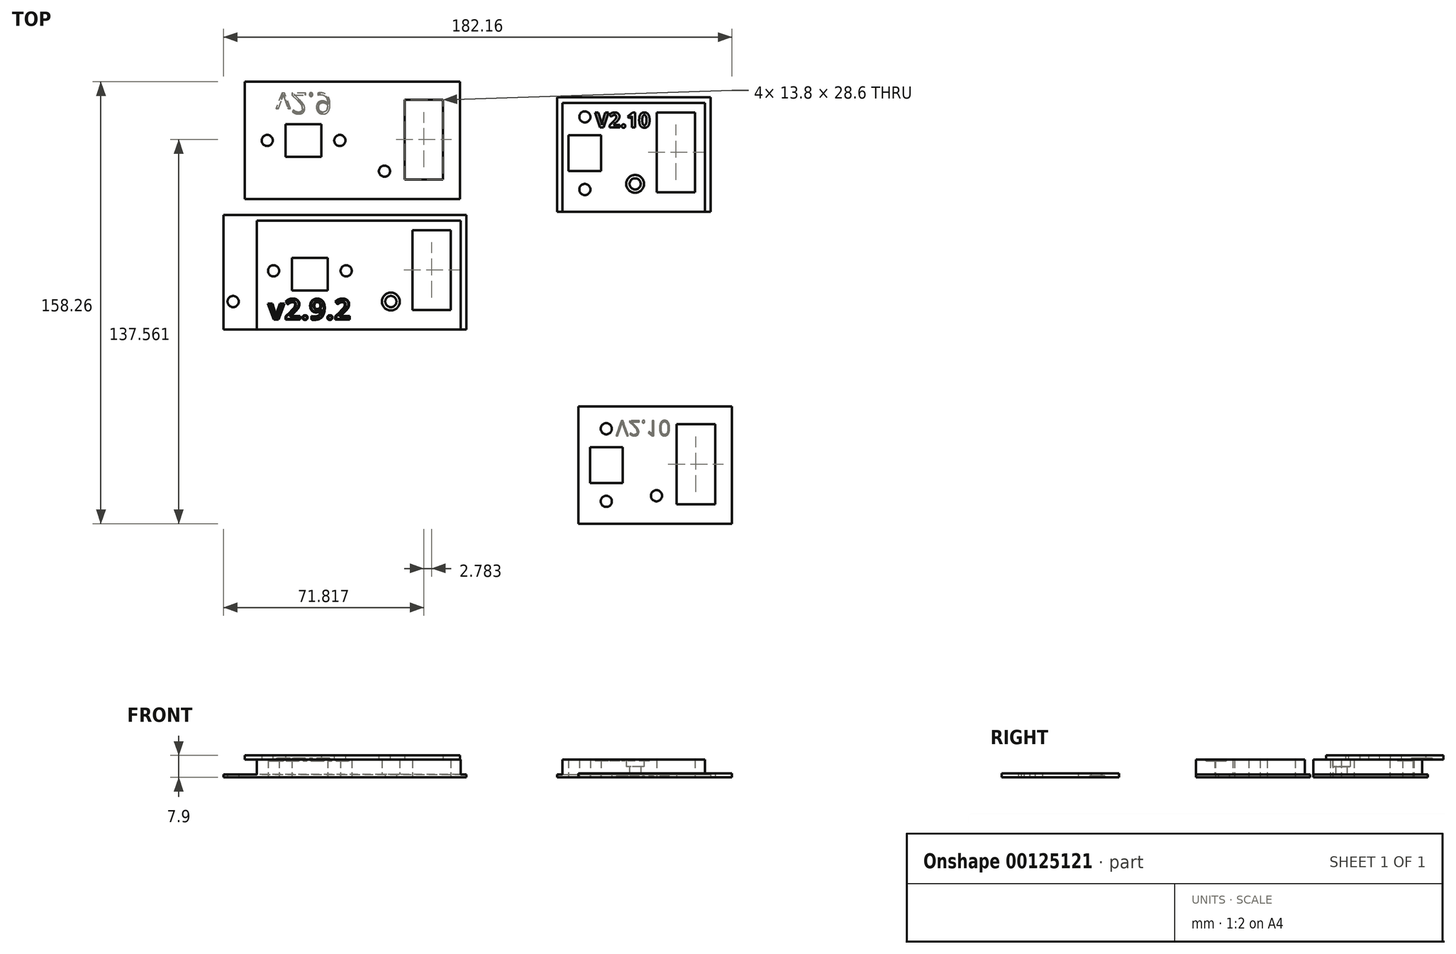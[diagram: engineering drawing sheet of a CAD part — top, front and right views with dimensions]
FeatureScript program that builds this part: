
annotation { "Feature Type Name" : "Feature", "Feature Type Description" : "" }
export const myFeature = defineFeature(function(context is Context, id is Id, definition is map)
    precondition{}
    {
        {
            var Q0;
            Q0=qCreatedBy(makeId("Top.planeOp"),FACE);
            var sketch = newSketch(context, id + "F0", { "sketchPlane" : qUnion([Q0])});
            skLineSegment(sketch, "E0.bottom", {"start": v(-50.93, -1.14) * mm, "end": v(36.07, -1.14) * mm});
            skLineSegment(sketch, "E0.left", {"start": v(-50.93, -1.14) * mm, "end": v(-50.93, -42.14) * mm});
            skLineSegment(sketch, "E0.right", {"start": v(36.07, -1.14) * mm, "end": v(36.07, -42.14) * mm});
            skLineSegment(sketch, "E1", {"start": v(-50.93, -42.14) * mm, "end": v(-38.93, -42.14) * mm});
            skLineSegment(sketch, "E2", {"start": v(-38.93, -42.14) * mm, "end": v(-32.93, -42.14) * mm});
            skLineSegment(sketch, "E3", {"start": v(-32.93, -42.14) * mm, "end": v(-6.93, -42.14) * mm});
            skLineSegment(sketch, "E4", {"start": v(-6.93, -42.14) * mm, "end": v(9.07, -42.14) * mm});
            skLineSegment(sketch, "E5", {"start": v(9.07, -42.14) * mm, "end": v(34.07, -42.14) * mm});
            skLineSegment(sketch, "E6", {"start": v(34.07, -42.14) * mm, "end": v(36.07, -42.14) * mm});
            skLineSegment(sketch, "E7", {"start": v(34.07, -42.14) * mm, "end": v(34.07, -3.14) * mm});
            skLineSegment(sketch, "E8", {"start": v(34.07, -3.14) * mm, "end": v(-38.93, -3.14) * mm});
            skLineSegment(sketch, "E9", {"start": v(-38.93, -3.14) * mm, "end": v(-38.93, -42.14) * mm});
            skLineSegment(sketch, "E10", {"start": v(-38.93, -42.14) * mm, "end": v(-47.43, -42.14) * mm, "construction": true});
            skLineSegment(sketch, "E11", {"start": v(-47.43, -42.14) * mm, "end": v(-47.43, -32.14) * mm, "construction": true});
            skCircle(sketch, "E12", {"center": v(-47.43, -32.14) * mm, "radius": 2 * mm});
            skLineSegment(sketch, "E13", {"start": v(-32.93, -42.14) * mm, "end": v(-32.93, -21.14) * mm, "construction": true});
            skLineSegment(sketch, "E14", {"start": v(-6.93, -42.14) * mm, "end": v(-6.93, -21.14) * mm, "construction": true});
            skLineSegment(sketch, "E15", {"start": v(9.07, -42.14) * mm, "end": v(9.07, -32.14) * mm, "construction": true});
            skCircle(sketch, "E16", {"center": v(9.07, -32.14) * mm, "radius": 2 * mm});
            skCircle(sketch, "E17", {"center": v(-32.93, -21.14) * mm, "radius": 2 * mm});
            skCircle(sketch, "E18", {"center": v(-6.93, -21.14) * mm, "radius": 2 * mm});
            skLineSegment(sketch, "E19.bottom", {"start": v(-26.33, -16.54) * mm, "end": v(-13.53, -16.54) * mm});
            skLineSegment(sketch, "E19.top", {"start": v(-26.33, -28.24) * mm, "end": v(-13.53, -28.24) * mm});
            skLineSegment(sketch, "E19.left", {"start": v(-26.33, -16.54) * mm, "end": v(-26.33, -28.24) * mm});
            skLineSegment(sketch, "E19.right", {"start": v(-13.53, -16.54) * mm, "end": v(-13.53, -28.24) * mm});
            skLineSegment(sketch, "E20", {"start": v(-32.93, -21.14) * mm, "end": v(-26.33, -21.14) * mm, "construction": true});
            skLineSegment(sketch, "E21", {"start": v(-6.93, -21.14) * mm, "end": v(-13.53, -21.14) * mm, "construction": true});
            skLineSegment(sketch, "E22", {"start": v(-19.93, -28.24) * mm, "end": v(-19.93, -42.14) * mm, "construction": true});
            skLineSegment(sketch, "E23.bottom", {"start": v(16.77, -6.54) * mm, "end": v(30.57, -6.54) * mm});
            skLineSegment(sketch, "E23.top", {"start": v(16.77, -35.14) * mm, "end": v(30.57, -35.14) * mm});
            skLineSegment(sketch, "E23.left", {"start": v(16.77, -6.54) * mm, "end": v(16.77, -35.14) * mm});
            skLineSegment(sketch, "E23.right", {"start": v(30.57, -6.54) * mm, "end": v(30.57, -35.14) * mm});
            skLineSegment(sketch, "E24", {"start": v(34.07, -42.14) * mm, "end": v(30.57, -42.14) * mm, "construction": true});
            skLineSegment(sketch, "E25", {"start": v(30.57, -42.14) * mm, "end": v(30.57, -35.14) * mm, "construction": true});
            skSolve(sketch);
        }
        {
            var Q0;
            Q0 = qSketchRegion(id + "F0", true);
            extrude(context, id + "F1", {"entities" : qUnion([Q0]), "depth" : 1 * mm});
        }
        {
            var Q0;
            Q0=makeQuery(id+"F1.opExtrude","CAP_FACE",FACE,{"disambiguationData":[OSD([sQuery(id+"F0.wireOp",EDGE,"E0.bottom"),sQuery(id+"F0.wireOp",EDGE,"E0.left"),sQuery(id+"F0.wireOp",EDGE,"E0.right"),sQuery(id+"F0.wireOp",EDGE,"E1"),sQuery(id+"F0.wireOp",EDGE,"E2"),sQuery(id+"F0.wireOp",EDGE,"E3"),sQuery(id+"F0.wireOp",EDGE,"E4"),sQuery(id+"F0.wireOp",EDGE,"E5"),sQuery(id+"F0.wireOp",EDGE,"E6"),sQuery(id+"F0.wireOp",EDGE,"E12"),sQuery(id+"F0.wireOp",EDGE,"E16"),sQuery(id+"F0.wireOp",EDGE,"E17"),sQuery(id+"F0.wireOp",EDGE,"E18"),sQuery(id+"F0.wireOp",EDGE,"E19.bottom"),sQuery(id+"F0.wireOp",EDGE,"E19.top"),sQuery(id+"F0.wireOp",EDGE,"E19.left"),sQuery(id+"F0.wireOp",EDGE,"E19.right"),sQuery(id+"F0.wireOp",EDGE,"E23.bottom"),sQuery(id+"F0.wireOp",EDGE,"E23.top"),sQuery(id+"F0.wireOp",EDGE,"E23.left"),sQuery(id+"F0.wireOp",EDGE,"E23.right")])],"isStart":false});
            var sketch = newSketch(context, id + "F2", { "sketchPlane" : qUnion([Q0])});
            skLineSegment(sketch, "E26.0", {"start": v(-38.93, -3.14) * mm, "end": v(-38.93, -42.14) * mm});
            skLineSegment(sketch, "E27.0", {"start": v(34.07, -3.14) * mm, "end": v(-38.93, -3.14) * mm});
            skLineSegment(sketch, "E28.0", {"start": v(34.07, -42.14) * mm, "end": v(34.07, -3.14) * mm});
            skLineSegment(sketch, "E29", {"start": v(-38.93, -42.14) * mm, "end": v(34.07, -42.14) * mm});
            skCircle(sketch, "E30.0", {"center": v(-32.93, -21.14) * mm, "radius": 2 * mm});
            skLineSegment(sketch, "E31.0", {"start": v(-26.33, -16.54) * mm, "end": v(-13.53, -16.54) * mm});
            skLineSegment(sketch, "E32.0", {"start": v(-13.53, -16.54) * mm, "end": v(-13.53, -28.24) * mm});
            skLineSegment(sketch, "E33.0", {"start": v(-26.33, -28.24) * mm, "end": v(-13.53, -28.24) * mm});
            skLineSegment(sketch, "E34.0", {"start": v(-26.33, -16.54) * mm, "end": v(-26.33, -28.24) * mm});
            skCircle(sketch, "E35.0", {"center": v(-6.93, -21.14) * mm, "radius": 2 * mm});
            skCircle(sketch, "E36.0", {"center": v(9.07, -32.14) * mm, "radius": 3.2 * mm});
            skLineSegment(sketch, "E37.0.0", {"start": v(30.57, -6.54) * mm, "end": v(16.77, -6.54) * mm});
            skLineSegment(sketch, "E37.0.1", {"start": v(16.77, -6.54) * mm, "end": v(16.77, -35.14) * mm});
            skLineSegment(sketch, "E37.0.2", {"start": v(16.77, -35.14) * mm, "end": v(30.57, -35.14) * mm});
            skLineSegment(sketch, "E37.0.3", {"start": v(30.57, -35.14) * mm, "end": v(30.57, -6.54) * mm});
            skSolve(sketch);
        }
        {
            var Q0;
            Q0 = qSketchRegion(id + "F2", true);
            extrude(context, id + "F3", {"entities" : qUnion([Q0]), "operationType" : NewBodyOperationType.ADD, "depth" : 5.4 * mm});
        }
        {
            var Q0;
            Q0=makeQuery(id+"F3.opExtrude","CAP_FACE",FACE,{"disambiguationData":[OSD([sQuery(id+"F2.wireOp",EDGE,"E26.0"),sQuery(id+"F2.wireOp",EDGE,"E27.0"),sQuery(id+"F2.wireOp",EDGE,"E28.0"),sQuery(id+"F2.wireOp",EDGE,"E29"),sQuery(id+"F2.wireOp",EDGE,"E30.0"),sQuery(id+"F2.wireOp",EDGE,"E31.0"),sQuery(id+"F2.wireOp",EDGE,"E32.0"),sQuery(id+"F2.wireOp",EDGE,"E33.0"),sQuery(id+"F2.wireOp",EDGE,"E34.0"),sQuery(id+"F2.wireOp",EDGE,"E35.0"),sQuery(id+"F2.wireOp",EDGE,"E36.0"),sQuery(id+"F2.wireOp",EDGE,"E37.0.0"),sQuery(id+"F2.wireOp",EDGE,"E37.0.1"),sQuery(id+"F2.wireOp",EDGE,"E37.0.2"),sQuery(id+"F2.wireOp",EDGE,"E37.0.3")])],"isStart":false});
            var sketch = newSketch(context, id + "F4", { "sketchPlane" : qUnion([Q0])});
            skText(sketch, "E38", { "text": "v2.9.2", "fontName": "OpenSans-Bold.ttf"});
            const initialGuessF4  = {"E38": [-0.035, -0.0386, 1, 0, 0.00749]};
            skSetInitialGuess(sketch, initialGuessF4);
            skSolve(sketch);
        }
        {
            var Q0;
            Q0 = qSketchRegion(id + "F4", true);
            extrude(context, id + "F5", {"entities" : qUnion([Q0]), "operationType" : NewBodyOperationType.REMOVE, "oppositeDirection" : true, "depth" : .5 * mm});
        }
        {
            var Q0;
            Q0=makeQuery(id+"F5.boolean.opBoolean","COPY",FACE,{"derivedFrom":makeQuery(id+"F5.opExtrude","CAP_FACE",FACE,{"disambiguationData":[OSD([sQuery(id+"F4.wireOp",EDGE,"E38.sketch_text.stroke-0"),sQuery(id+"F4.wireOp",EDGE,"E38.sketch_text.stroke-1"),sQuery(id+"F4.wireOp",EDGE,"E38.sketch_text.stroke-2"),sQuery(id+"F4.wireOp",EDGE,"E38.sketch_text.stroke-3"),sQuery(id+"F4.wireOp",EDGE,"E38.sketch_text.stroke-4"),sQuery(id+"F4.wireOp",EDGE,"E38.sketch_text.stroke-5"),sQuery(id+"F4.wireOp",EDGE,"E38.sketch_text.stroke-6"),sQuery(id+"F4.wireOp",EDGE,"E38.sketch_text.stroke-7"),sQuery(id+"F4.wireOp",EDGE,"E38.sketch_text.stroke-8"),sQuery(id+"F4.wireOp",EDGE,"E38.sketch_text.stroke-9")])],"isStart":false})});
            var Q1;
            Q1=makeQuery(id+"F5.boolean.opBoolean","COPY",FACE,{"derivedFrom":makeQuery(id+"F5.opExtrude","CAP_FACE",FACE,{"disambiguationData":[OSD([sQuery(id+"F4.wireOp",EDGE,"E38.sketch_text.stroke-10"),sQuery(id+"F4.wireOp",EDGE,"E38.sketch_text.stroke-11"),sQuery(id+"F4.wireOp",EDGE,"E38.sketch_text.stroke-12"),sQuery(id+"F4.wireOp",EDGE,"E38.sketch_text.stroke-13"),sQuery(id+"F4.wireOp",EDGE,"E38.sketch_text.stroke-14"),sQuery(id+"F4.wireOp",EDGE,"E38.sketch_text.stroke-15"),sQuery(id+"F4.wireOp",EDGE,"E38.sketch_text.stroke-16"),sQuery(id+"F4.wireOp",EDGE,"E38.sketch_text.stroke-17"),sQuery(id+"F4.wireOp",EDGE,"E38.sketch_text.stroke-18"),sQuery(id+"F4.wireOp",EDGE,"E38.sketch_text.stroke-19"),sQuery(id+"F4.wireOp",EDGE,"E38.sketch_text.stroke-20"),sQuery(id+"F4.wireOp",EDGE,"E38.sketch_text.stroke-21"),sQuery(id+"F4.wireOp",EDGE,"E38.sketch_text.stroke-22"),sQuery(id+"F4.wireOp",EDGE,"E38.sketch_text.stroke-23"),sQuery(id+"F4.wireOp",EDGE,"E38.sketch_text.stroke-24"),sQuery(id+"F4.wireOp",EDGE,"E38.sketch_text.stroke-25"),sQuery(id+"F4.wireOp",EDGE,"E38.sketch_text.stroke-26"),sQuery(id+"F4.wireOp",EDGE,"E38.sketch_text.stroke-27"),sQuery(id+"F4.wireOp",EDGE,"E38.sketch_text.stroke-28"),sQuery(id+"F4.wireOp",EDGE,"E38.sketch_text.stroke-29"),sQuery(id+"F4.wireOp",EDGE,"E38.sketch_text.stroke-30"),sQuery(id+"F4.wireOp",EDGE,"E38.sketch_text.stroke-31"),sQuery(id+"F4.wireOp",EDGE,"E38.sketch_text.stroke-32"),sQuery(id+"F4.wireOp",EDGE,"E38.sketch_text.stroke-33")])],"isStart":false})});
            var Q2;
            Q2=makeQuery(id+"F5.boolean.opBoolean","COPY",FACE,{"derivedFrom":makeQuery(id+"F5.opExtrude","CAP_FACE",FACE,{"disambiguationData":[OSD([sQuery(id+"F4.wireOp",EDGE,"E38.sketch_text.stroke-34"),sQuery(id+"F4.wireOp",EDGE,"E38.sketch_text.stroke-35"),sQuery(id+"F4.wireOp",EDGE,"E38.sketch_text.stroke-36"),sQuery(id+"F4.wireOp",EDGE,"E38.sketch_text.stroke-37"),sQuery(id+"F4.wireOp",EDGE,"E38.sketch_text.stroke-38"),sQuery(id+"F4.wireOp",EDGE,"E38.sketch_text.stroke-39"),sQuery(id+"F4.wireOp",EDGE,"E38.sketch_text.stroke-40"),sQuery(id+"F4.wireOp",EDGE,"E38.sketch_text.stroke-41")])],"isStart":false})});
            var Q3;
            Q3=makeQuery(id+"F5.boolean.opBoolean","COPY",FACE,{"derivedFrom":makeQuery(id+"F5.opExtrude","CAP_FACE",FACE,{"disambiguationData":[OSD([sQuery(id+"F4.wireOp",EDGE,"E38.sketch_text.stroke-42"),sQuery(id+"F4.wireOp",EDGE,"E38.sketch_text.stroke-43"),sQuery(id+"F4.wireOp",EDGE,"E38.sketch_text.stroke-44"),sQuery(id+"F4.wireOp",EDGE,"E38.sketch_text.stroke-45"),sQuery(id+"F4.wireOp",EDGE,"E38.sketch_text.stroke-46"),sQuery(id+"F4.wireOp",EDGE,"E38.sketch_text.stroke-47"),sQuery(id+"F4.wireOp",EDGE,"E38.sketch_text.stroke-48"),sQuery(id+"F4.wireOp",EDGE,"E38.sketch_text.stroke-49"),sQuery(id+"F4.wireOp",EDGE,"E38.sketch_text.stroke-50"),sQuery(id+"F4.wireOp",EDGE,"E38.sketch_text.stroke-51"),sQuery(id+"F4.wireOp",EDGE,"E38.sketch_text.stroke-52"),sQuery(id+"F4.wireOp",EDGE,"E38.sketch_text.stroke-53"),sQuery(id+"F4.wireOp",EDGE,"E38.sketch_text.stroke-54"),sQuery(id+"F4.wireOp",EDGE,"E38.sketch_text.stroke-55"),sQuery(id+"F4.wireOp",EDGE,"E38.sketch_text.stroke-56"),sQuery(id+"F4.wireOp",EDGE,"E38.sketch_text.stroke-57"),sQuery(id+"F4.wireOp",EDGE,"E38.sketch_text.stroke-58"),sQuery(id+"F4.wireOp",EDGE,"E38.sketch_text.stroke-59"),sQuery(id+"F4.wireOp",EDGE,"E38.sketch_text.stroke-60"),sQuery(id+"F4.wireOp",EDGE,"E38.sketch_text.stroke-61"),sQuery(id+"F4.wireOp",EDGE,"E38.sketch_text.stroke-62"),sQuery(id+"F4.wireOp",EDGE,"E38.sketch_text.stroke-63"),sQuery(id+"F4.wireOp",EDGE,"E38.sketch_text.stroke-64"),sQuery(id+"F4.wireOp",EDGE,"E38.sketch_text.stroke-65"),sQuery(id+"F4.wireOp",EDGE,"E38.sketch_text.stroke-66"),sQuery(id+"F4.wireOp",EDGE,"E38.sketch_text.stroke-67")])],"isStart":false})});
            var Q4;
            Q4=makeQuery(id+"F5.boolean.opBoolean","COPY",FACE,{"derivedFrom":makeQuery(id+"F5.opExtrude","CAP_FACE",FACE,{"disambiguationData":[OSD([sQuery(id+"F4.wireOp",EDGE,"E38.sketch_text.stroke-68"),sQuery(id+"F4.wireOp",EDGE,"E38.sketch_text.stroke-69"),sQuery(id+"F4.wireOp",EDGE,"E38.sketch_text.stroke-70"),sQuery(id+"F4.wireOp",EDGE,"E38.sketch_text.stroke-71"),sQuery(id+"F4.wireOp",EDGE,"E38.sketch_text.stroke-72"),sQuery(id+"F4.wireOp",EDGE,"E38.sketch_text.stroke-73"),sQuery(id+"F4.wireOp",EDGE,"E38.sketch_text.stroke-74"),sQuery(id+"F4.wireOp",EDGE,"E38.sketch_text.stroke-75")])],"isStart":false})});
            var Q5;
            Q5=makeQuery(id+"F5.boolean.opBoolean","COPY",FACE,{"derivedFrom":makeQuery(id+"F5.opExtrude","CAP_FACE",FACE,{"disambiguationData":[OSD([sQuery(id+"F4.wireOp",EDGE,"E38.sketch_text.stroke-76"),sQuery(id+"F4.wireOp",EDGE,"E38.sketch_text.stroke-77"),sQuery(id+"F4.wireOp",EDGE,"E38.sketch_text.stroke-78"),sQuery(id+"F4.wireOp",EDGE,"E38.sketch_text.stroke-79"),sQuery(id+"F4.wireOp",EDGE,"E38.sketch_text.stroke-80"),sQuery(id+"F4.wireOp",EDGE,"E38.sketch_text.stroke-81"),sQuery(id+"F4.wireOp",EDGE,"E38.sketch_text.stroke-82"),sQuery(id+"F4.wireOp",EDGE,"E38.sketch_text.stroke-83"),sQuery(id+"F4.wireOp",EDGE,"E38.sketch_text.stroke-84"),sQuery(id+"F4.wireOp",EDGE,"E38.sketch_text.stroke-85")])],"isStart":false})});
            chamfer(context, id + "F6", {"entities" : qUnion([Q0, Q1, Q2, Q3, Q4, Q5]), "width" : .3 * mm, "tangentPropagation" : true});
        }
        {
            var Q0;
            {var subQ0=sQuery(id+"F2.wireOp",EDGE,"E36.0");var subQ1=sQuery(id+"F2.wireOp",EDGE,"E33.0");var subQ2=sQuery(id+"F2.wireOp",EDGE,"E29");var subQ3=sQuery(id+"F2.wireOp",EDGE,"E32.0");var subQ4=sQuery(id+"F2.wireOp",EDGE,"E28.0");var subQ5=sQuery(id+"F2.wireOp",EDGE,"E34.0");var subQ6=sQuery(id+"F2.wireOp",EDGE,"E31.0");var subQ7=sQuery(id+"F2.wireOp",EDGE,"E30.0");var subQ8=sQuery(id+"F2.wireOp",EDGE,"E26.0");var subQ9=sQuery(id+"F2.wireOp",EDGE,"E37.0.2");var subQ10=sQuery(id+"F2.wireOp",EDGE,"E27.0");var subQ11=sQuery(id+"F2.wireOp",EDGE,"E37.0.0");var subQ12=sQuery(id+"F2.wireOp",EDGE,"E37.0.1");var subQ13=sQuery(id+"F2.wireOp",EDGE,"E37.0.3");var subQ14=sQuery(id+"F2.wireOp",EDGE,"E35.0");Q0=makeQuery(id+"F5.boolean.opBoolean","SPLIT",FACE,{"disambiguationData":[TD([makeQuery(id+"F1.opExtrude","SWEPT_FACE",FACE,{"disambiguationData":[OSD([sQuery(id+"F0.wireOp",EDGE,"E17")])]})])],"derivedFrom":makeQuery(id+"F3.opExtrude","CAP_FACE",FACE,{"disambiguationData":[OSD([subQ8,subQ10,subQ4,subQ2,subQ7,subQ6,subQ3,subQ1,subQ5,subQ14,subQ0,subQ11,subQ12,subQ9,subQ13])],"isStart":false})});}
            var sketch = newSketch(context, id + "F7", { "sketchPlane" : qUnion([Q0])});
            skLineSegment(sketch, "E39.bottom", {"start": v(-43.21, -4.27) * mm, "end": v(33.79, -4.27) * mm});
            skLineSegment(sketch, "E39.left", {"start": v(-43.21, -4.27) * mm, "end": v(-43.21, -46.27) * mm});
            skLineSegment(sketch, "E39.right", {"start": v(33.79, -4.27) * mm, "end": v(33.79, -46.27) * mm});
            skLineSegment(sketch, "E40", {"start": v(-43.21, -46.27) * mm, "end": v(-35.21, -46.27) * mm});
            skLineSegment(sketch, "E41", {"start": v(-35.21, -46.27) * mm, "end": v(-9.21, -46.27) * mm});
            skLineSegment(sketch, "E42", {"start": v(-9.21, -46.27) * mm, "end": v(6.79, -46.27) * mm});
            skLineSegment(sketch, "E43", {"start": v(6.79, -46.27) * mm, "end": v(27.79, -46.27) * mm});
            skLineSegment(sketch, "E44", {"start": v(27.79, -46.27) * mm, "end": v(33.79, -46.27) * mm});
            skLineSegment(sketch, "E45", {"start": v(27.79, -46.27) * mm, "end": v(27.79, -39.27) * mm, "construction": true});
            skLineSegment(sketch, "E46.0", {"start": v(-28.61, -19.42) * mm, "end": v(-28.61, -31.12) * mm});
            skLineSegment(sketch, "E47.0", {"start": v(-28.61, -19.42) * mm, "end": v(-15.81, -19.42) * mm});
            skLineSegment(sketch, "E48.0", {"start": v(-15.81, -19.42) * mm, "end": v(-15.81, -31.12) * mm});
            skLineSegment(sketch, "E49.0", {"start": v(-28.61, -31.12) * mm, "end": v(-15.81, -31.12) * mm});
            skLineSegment(sketch, "E50.0", {"start": v(13.99, -10.67) * mm, "end": v(13.99, -39.27) * mm});
            skLineSegment(sketch, "E51.0", {"start": v(13.99, -10.67) * mm, "end": v(27.79, -10.67) * mm});
            skLineSegment(sketch, "E52.0", {"start": v(27.79, -10.67) * mm, "end": v(27.79, -39.27) * mm});
            skLineSegment(sketch, "E53.0", {"start": v(13.99, -39.27) * mm, "end": v(27.79, -39.27) * mm});
            skLineSegment(sketch, "E54", {"start": v(-28.61, -25.27) * mm, "end": v(-15.81, -25.27) * mm, "construction": true});
            skLineSegment(sketch, "E55", {"start": v(-35.21, -46.27) * mm, "end": v(-35.21, -25.27) * mm, "construction": true});
            skLineSegment(sketch, "E56", {"start": v(-9.21, -46.27) * mm, "end": v(-9.21, -25.27) * mm, "construction": true});
            skLineSegment(sketch, "E57", {"start": v(-35.21, -25.27) * mm, "end": v(-28.61, -25.27) * mm, "construction": true});
            skLineSegment(sketch, "E58", {"start": v(-15.81, -25.27) * mm, "end": v(-9.21, -25.27) * mm, "construction": true});
            skCircle(sketch, "E59", {"center": v(-35.21, -25.27) * mm, "radius": 2 * mm});
            skCircle(sketch, "E60", {"center": v(-9.21, -25.27) * mm, "radius": 2 * mm});
            skLineSegment(sketch, "E61", {"start": v(6.79, -46.27) * mm, "end": v(6.79, -36.27) * mm, "construction": true});
            skCircle(sketch, "E62", {"center": v(6.79, -36.27) * mm, "radius": 2 * mm});
            skSolve(sketch);
        }
        {
            var Q0;
            Q0 = qSketchRegion(id + "F7", true);
            extrude(context, id + "F8", {"entities" : qUnion([Q0]), "depth" : 1.5 * mm});
        }
        {
            var Q0;
            Q0=makeQuery(id+"F8.opExtrude","SWEPT_BODY",BODY,{"disambiguationData":[OSD([sQuery(id+"F7.wireOp",EDGE,"E39.bottom"),sQuery(id+"F7.wireOp",EDGE,"E39.left"),sQuery(id+"F7.wireOp",EDGE,"E39.right"),sQuery(id+"F7.wireOp",EDGE,"E40"),sQuery(id+"F7.wireOp",EDGE,"E41"),sQuery(id+"F7.wireOp",EDGE,"E42"),sQuery(id+"F7.wireOp",EDGE,"E43"),sQuery(id+"F7.wireOp",EDGE,"E44"),sQuery(id+"F7.wireOp",EDGE,"E46.0"),sQuery(id+"F7.wireOp",EDGE,"E47.0"),sQuery(id+"F7.wireOp",EDGE,"E48.0"),sQuery(id+"F7.wireOp",EDGE,"E49.0"),sQuery(id+"F7.wireOp",EDGE,"E50.0"),sQuery(id+"F7.wireOp",EDGE,"E51.0"),sQuery(id+"F7.wireOp",EDGE,"E52.0"),sQuery(id+"F7.wireOp",EDGE,"E53.0"),sQuery(id+"F7.wireOp",EDGE,"E59"),sQuery(id+"F7.wireOp",EDGE,"E60")])]});
            transform(context, id + "F9", {"entities" : qUnion([Q0]), "transformType" : TransformType.TRANSLATION_3D, "dx" : 0 * mm, "dy" : 50.83 * mm, "dz" : 0 * mm, "makeCopy" : false});
        }
        {
            var Q0;
            Q0=makeQuery(id+"F8.opExtrude","CAP_FACE",FACE,{"disambiguationData":[OSD([sQuery(id+"F7.wireOp",EDGE,"E39.bottom"),sQuery(id+"F7.wireOp",EDGE,"E39.left"),sQuery(id+"F7.wireOp",EDGE,"E39.right"),sQuery(id+"F7.wireOp",EDGE,"E40"),sQuery(id+"F7.wireOp",EDGE,"E41"),sQuery(id+"F7.wireOp",EDGE,"E42"),sQuery(id+"F7.wireOp",EDGE,"E43"),sQuery(id+"F7.wireOp",EDGE,"E44"),sQuery(id+"F7.wireOp",EDGE,"E46.0"),sQuery(id+"F7.wireOp",EDGE,"E47.0"),sQuery(id+"F7.wireOp",EDGE,"E48.0"),sQuery(id+"F7.wireOp",EDGE,"E49.0"),sQuery(id+"F7.wireOp",EDGE,"E50.0"),sQuery(id+"F7.wireOp",EDGE,"E51.0"),sQuery(id+"F7.wireOp",EDGE,"E52.0"),sQuery(id+"F7.wireOp",EDGE,"E53.0"),sQuery(id+"F7.wireOp",EDGE,"E59"),sQuery(id+"F7.wireOp",EDGE,"E60")])],"isStart":true});
            var sketch = newSketch(context, id + "F10", { "sketchPlane" : qUnion([Q0])});
            skText(sketch, "E63", { "text": "v2.9", "fontName": "OpenSans-Regular.ttf"});
            const initialGuessF10  = {"E63": [-0.03207, -0.04255, 1, 0, 0.0075]};
            skSetInitialGuess(sketch, initialGuessF10);
            skSolve(sketch);
        }
        {
            var Q0;
            Q0 = qSketchRegion(id + "F10", true);
            extrude(context, id + "F11", {"entities" : qUnion([Q0]), "operationType" : NewBodyOperationType.REMOVE, "oppositeDirection" : true, "depth" : .5 * mm});
        }
        {
            var Q0;
            Q0=makeQuery(id+"F11.boolean.opBoolean","COPY",FACE,{"derivedFrom":makeQuery(id+"F11.opExtrude","CAP_FACE",FACE,{"disambiguationData":[OSD([sQuery(id+"F10.wireOp",EDGE,"E63.sketch_text.stroke-38"),sQuery(id+"F10.wireOp",EDGE,"E63.sketch_text.stroke-39"),sQuery(id+"F10.wireOp",EDGE,"E63.sketch_text.stroke-40"),sQuery(id+"F10.wireOp",EDGE,"E63.sketch_text.stroke-41"),sQuery(id+"F10.wireOp",EDGE,"E63.sketch_text.stroke-42"),sQuery(id+"F10.wireOp",EDGE,"E63.sketch_text.stroke-43"),sQuery(id+"F10.wireOp",EDGE,"E63.sketch_text.stroke-44"),sQuery(id+"F10.wireOp",EDGE,"E63.sketch_text.stroke-45"),sQuery(id+"F10.wireOp",EDGE,"E63.sketch_text.stroke-46"),sQuery(id+"F10.wireOp",EDGE,"E63.sketch_text.stroke-47"),sQuery(id+"F10.wireOp",EDGE,"E63.sketch_text.stroke-48"),sQuery(id+"F10.wireOp",EDGE,"E63.sketch_text.stroke-49"),sQuery(id+"F10.wireOp",EDGE,"E63.sketch_text.stroke-50"),sQuery(id+"F10.wireOp",EDGE,"E63.sketch_text.stroke-51"),sQuery(id+"F10.wireOp",EDGE,"E63.sketch_text.stroke-52"),sQuery(id+"F10.wireOp",EDGE,"E63.sketch_text.stroke-53"),sQuery(id+"F10.wireOp",EDGE,"E63.sketch_text.stroke-54"),sQuery(id+"F10.wireOp",EDGE,"E63.sketch_text.stroke-55"),sQuery(id+"F10.wireOp",EDGE,"E63.sketch_text.stroke-56"),sQuery(id+"F10.wireOp",EDGE,"E63.sketch_text.stroke-57"),sQuery(id+"F10.wireOp",EDGE,"E63.sketch_text.stroke-58"),sQuery(id+"F10.wireOp",EDGE,"E63.sketch_text.stroke-59"),sQuery(id+"F10.wireOp",EDGE,"E63.sketch_text.stroke-60"),sQuery(id+"F10.wireOp",EDGE,"E63.sketch_text.stroke-61"),sQuery(id+"F10.wireOp",EDGE,"E63.sketch_text.stroke-62"),sQuery(id+"F10.wireOp",EDGE,"E63.sketch_text.stroke-63")])],"isStart":false})});
            var Q1;
            Q1=makeQuery(id+"F11.boolean.opBoolean","COPY",FACE,{"derivedFrom":makeQuery(id+"F11.opExtrude","CAP_FACE",FACE,{"disambiguationData":[OSD([sQuery(id+"F10.wireOp",EDGE,"E63.sketch_text.stroke-30"),sQuery(id+"F10.wireOp",EDGE,"E63.sketch_text.stroke-31"),sQuery(id+"F10.wireOp",EDGE,"E63.sketch_text.stroke-32"),sQuery(id+"F10.wireOp",EDGE,"E63.sketch_text.stroke-33"),sQuery(id+"F10.wireOp",EDGE,"E63.sketch_text.stroke-34"),sQuery(id+"F10.wireOp",EDGE,"E63.sketch_text.stroke-35"),sQuery(id+"F10.wireOp",EDGE,"E63.sketch_text.stroke-36"),sQuery(id+"F10.wireOp",EDGE,"E63.sketch_text.stroke-37")])],"isStart":false})});
            var Q2;
            Q2=makeQuery(id+"F11.boolean.opBoolean","COPY",FACE,{"derivedFrom":makeQuery(id+"F11.opExtrude","CAP_FACE",FACE,{"disambiguationData":[OSD([sQuery(id+"F10.wireOp",EDGE,"E63.sketch_text.stroke-10"),sQuery(id+"F10.wireOp",EDGE,"E63.sketch_text.stroke-11"),sQuery(id+"F10.wireOp",EDGE,"E63.sketch_text.stroke-12"),sQuery(id+"F10.wireOp",EDGE,"E63.sketch_text.stroke-13"),sQuery(id+"F10.wireOp",EDGE,"E63.sketch_text.stroke-14"),sQuery(id+"F10.wireOp",EDGE,"E63.sketch_text.stroke-15"),sQuery(id+"F10.wireOp",EDGE,"E63.sketch_text.stroke-16"),sQuery(id+"F10.wireOp",EDGE,"E63.sketch_text.stroke-17"),sQuery(id+"F10.wireOp",EDGE,"E63.sketch_text.stroke-18"),sQuery(id+"F10.wireOp",EDGE,"E63.sketch_text.stroke-19"),sQuery(id+"F10.wireOp",EDGE,"E63.sketch_text.stroke-20"),sQuery(id+"F10.wireOp",EDGE,"E63.sketch_text.stroke-21"),sQuery(id+"F10.wireOp",EDGE,"E63.sketch_text.stroke-22"),sQuery(id+"F10.wireOp",EDGE,"E63.sketch_text.stroke-23"),sQuery(id+"F10.wireOp",EDGE,"E63.sketch_text.stroke-24"),sQuery(id+"F10.wireOp",EDGE,"E63.sketch_text.stroke-25"),sQuery(id+"F10.wireOp",EDGE,"E63.sketch_text.stroke-26"),sQuery(id+"F10.wireOp",EDGE,"E63.sketch_text.stroke-27"),sQuery(id+"F10.wireOp",EDGE,"E63.sketch_text.stroke-28"),sQuery(id+"F10.wireOp",EDGE,"E63.sketch_text.stroke-29")])],"isStart":false})});
            var Q3;
            Q3=makeQuery(id+"F11.boolean.opBoolean","COPY",FACE,{"derivedFrom":makeQuery(id+"F11.opExtrude","CAP_FACE",FACE,{"disambiguationData":[OSD([sQuery(id+"F10.wireOp",EDGE,"E63.sketch_text.stroke-0"),sQuery(id+"F10.wireOp",EDGE,"E63.sketch_text.stroke-1"),sQuery(id+"F10.wireOp",EDGE,"E63.sketch_text.stroke-2"),sQuery(id+"F10.wireOp",EDGE,"E63.sketch_text.stroke-3"),sQuery(id+"F10.wireOp",EDGE,"E63.sketch_text.stroke-4"),sQuery(id+"F10.wireOp",EDGE,"E63.sketch_text.stroke-5"),sQuery(id+"F10.wireOp",EDGE,"E63.sketch_text.stroke-6"),sQuery(id+"F10.wireOp",EDGE,"E63.sketch_text.stroke-7"),sQuery(id+"F10.wireOp",EDGE,"E63.sketch_text.stroke-8"),sQuery(id+"F10.wireOp",EDGE,"E63.sketch_text.stroke-9")])],"isStart":false})});
            fillet(context, id + "F12", {"entities" : qUnion([Q0, Q1, Q2, Q3]), "radius" : .3 * mm, "tangentPropagation" : true, "allowEdgeOverflow" : false});
        }
        {
            var Q0;
            Q0=qCreatedBy(makeId("Top.planeOp"),FACE);
            var sketch = newSketch(context, id + "F13", { "sketchPlane" : qUnion([Q0])});
            skLineSegment(sketch, "E64.bottom", {"start": v(68.57, 41) * mm, "end": v(123.57, 41) * mm});
            skLineSegment(sketch, "E64.top", {"start": v(68.57, 0) * mm, "end": v(123.57, 0) * mm});
            skLineSegment(sketch, "E64.left", {"start": v(68.57, 41) * mm, "end": v(68.57, 0) * mm});
            skLineSegment(sketch, "E64.right", {"start": v(123.57, 41) * mm, "end": v(123.57, 0) * mm});
            skLineSegment(sketch, "E65", {"start": v(68.57, 0) * mm, "end": v(70.57, 0) * mm, "construction": true});
            skLineSegment(sketch, "E66", {"start": v(70.57, 0) * mm, "end": v(70.57, 39) * mm, "construction": true});
            skLineSegment(sketch, "E67", {"start": v(70.57, 39) * mm, "end": v(121.57, 39) * mm, "construction": true});
            skLineSegment(sketch, "E68", {"start": v(121.57, 39) * mm, "end": v(121.57, 0) * mm, "construction": true});
            skLineSegment(sketch, "E69", {"start": v(70.57, 0) * mm, "end": v(78.57, 0) * mm, "construction": true});
            skLineSegment(sketch, "E70", {"start": v(78.57, 0) * mm, "end": v(78.57, 8) * mm, "construction": true});
            skLineSegment(sketch, "E71", {"start": v(78.57, 0) * mm, "end": v(96.57, 0) * mm, "construction": true});
            skLineSegment(sketch, "E72", {"start": v(96.57, 0) * mm, "end": v(96.57, 10) * mm, "construction": true});
            skLineSegment(sketch, "E73", {"start": v(96.57, 0) * mm, "end": v(118.07, 0) * mm, "construction": true});
            skLineSegment(sketch, "E74", {"start": v(118.07, 0) * mm, "end": v(118.07, 7) * mm, "construction": true});
            skLineSegment(sketch, "E75", {"start": v(70.57, 39) * mm, "end": v(70.57, 34) * mm, "construction": true});
            skLineSegment(sketch, "E76", {"start": v(70.57, 34) * mm, "end": v(70.57, 8) * mm, "construction": true});
            skLineSegment(sketch, "E77", {"start": v(70.57, 8) * mm, "end": v(70.57, 0) * mm, "construction": true});
            skLineSegment(sketch, "E78.bottom", {"start": v(118.07, 7) * mm, "end": v(104.27, 7) * mm});
            skLineSegment(sketch, "E78.top", {"start": v(118.07, 35.6) * mm, "end": v(104.27, 35.6) * mm});
            skLineSegment(sketch, "E78.left", {"start": v(118.07, 7) * mm, "end": v(118.07, 35.6) * mm});
            skLineSegment(sketch, "E78.right", {"start": v(104.27, 7) * mm, "end": v(104.27, 35.6) * mm});
            skLineSegment(sketch, "E79.bottom", {"start": v(72.72, 27.4) * mm, "end": v(84.42, 27.4) * mm});
            skLineSegment(sketch, "E79.top", {"start": v(72.72, 14.6) * mm, "end": v(84.42, 14.6) * mm});
            skLineSegment(sketch, "E79.left", {"start": v(72.72, 27.4) * mm, "end": v(72.72, 14.6) * mm});
            skLineSegment(sketch, "E79.right", {"start": v(84.42, 27.4) * mm, "end": v(84.42, 14.6) * mm});
            skPoint(sketch, "E80", {"position": v(72.72, 21) * mm});
            skPoint(sketch, "E81", {"position": v(70.57, 21) * mm});
            skLineSegment(sketch, "E82", {"start": v(70.57, 21) * mm, "end": v(72.72, 21) * mm});
            skLineSegment(sketch, "E83", {"start": v(78.57, 34) * mm, "end": v(70.57, 34) * mm, "construction": true});
            skCircle(sketch, "E84", {"center": v(78.57, 34) * mm, "radius": 2 * mm});
            skCircle(sketch, "E85", {"center": v(78.57, 8) * mm, "radius": 2 * mm});
            skCircle(sketch, "E86", {"center": v(96.57, 10) * mm, "radius": 2 * mm});
            skPoint(sketch, "E87", {"position": v(78.57, 27.4) * mm});
            skSolve(sketch);
        }
        {
            var Q0;
            Q0 = qSketchRegion(id + "F13", true);
            extrude(context, id + "F14", {"entities" : qUnion([Q0]), "depth" : 1 * mm});
        }
        {
            var Q0;
            Q0=makeQuery(id+"F14.opExtrude","CAP_FACE",FACE,{"disambiguationData":[OSD([sQuery(id+"F13.wireOp",EDGE,"E64.bottom"),sQuery(id+"F13.wireOp",EDGE,"E64.top"),sQuery(id+"F13.wireOp",EDGE,"E64.left"),sQuery(id+"F13.wireOp",EDGE,"E64.right"),sQuery(id+"F13.wireOp",EDGE,"E78.bottom"),sQuery(id+"F13.wireOp",EDGE,"E78.top"),sQuery(id+"F13.wireOp",EDGE,"E78.left"),sQuery(id+"F13.wireOp",EDGE,"E78.right"),sQuery(id+"F13.wireOp",EDGE,"E79.bottom"),sQuery(id+"F13.wireOp",EDGE,"E79.top"),sQuery(id+"F13.wireOp",EDGE,"E79.left"),sQuery(id+"F13.wireOp",EDGE,"E79.right"),sQuery(id+"F13.wireOp",EDGE,"E84"),sQuery(id+"F13.wireOp",EDGE,"E85"),sQuery(id+"F13.wireOp",EDGE,"E86")])],"isStart":false});
            var sketch = newSketch(context, id + "F15", { "sketchPlane" : qUnion([Q0])});
            skLineSegment(sketch, "E88.0", {"start": v(70.57, 34) * mm, "end": v(70.57, 8) * mm});
            skLineSegment(sketch, "E89.0", {"start": v(70.57, 39) * mm, "end": v(70.57, 34) * mm});
            skLineSegment(sketch, "E90.0", {"start": v(70.57, 8) * mm, "end": v(70.57, 0) * mm});
            skLineSegment(sketch, "E91.0", {"start": v(70.57, 39) * mm, "end": v(121.57, 39) * mm});
            skLineSegment(sketch, "E92.0", {"start": v(121.57, 39) * mm, "end": v(121.57, 0) * mm});
            skLineSegment(sketch, "E93.0", {"start": v(68.57, 0) * mm, "end": v(123.57, 0) * mm});
            skLineSegment(sketch, "E94.0", {"start": v(72.72, 14.6) * mm, "end": v(84.42, 14.6) * mm});
            skLineSegment(sketch, "E95.0", {"start": v(84.42, 27.4) * mm, "end": v(84.42, 14.6) * mm});
            skLineSegment(sketch, "E96.0", {"start": v(72.72, 27.4) * mm, "end": v(84.42, 27.4) * mm});
            skLineSegment(sketch, "E97.0", {"start": v(72.72, 27.4) * mm, "end": v(72.72, 14.6) * mm});
            skLineSegment(sketch, "E98.0.0", {"start": v(104.27, 7) * mm, "end": v(118.07, 7) * mm});
            skLineSegment(sketch, "E98.0.1", {"start": v(118.07, 7) * mm, "end": v(118.07, 35.6) * mm});
            skLineSegment(sketch, "E98.0.2", {"start": v(118.07, 35.6) * mm, "end": v(104.27, 35.6) * mm});
            skLineSegment(sketch, "E98.0.3", {"start": v(104.27, 35.6) * mm, "end": v(104.27, 7) * mm});
            skCircle(sketch, "E99.0", {"center": v(78.57, 8) * mm, "radius": 2 * mm});
            skCircle(sketch, "E100.0", {"center": v(78.57, 34) * mm, "radius": 2 * mm});
            skCircle(sketch, "E101", {"center": v(96.57, 10) * mm, "radius": 3.2 * mm});
            skSolve(sketch);
        }
        {
            var Q0;
            Q0 = qSketchRegion(id + "F15", true);
            extrude(context, id + "F16", {"entities" : qUnion([Q0]), "operationType" : NewBodyOperationType.ADD, "depth" : 5.4 * mm});
        }
        {
            var Q0;
            {var subQ0=sQuery(id+"F13.wireOp",EDGE,"E86");Q0=makeQuery(id+"F16.boolean.opBoolean","SPLIT",FACE,{"disambiguationData":[TD([makeQuery(id+"F14.opExtrude","SWEPT_FACE",FACE,{"disambiguationData":[OSD([subQ0])]})])],"derivedFrom":makeQuery(id+"F14.opExtrude","CAP_FACE",FACE,{"disambiguationData":[OSD([sQuery(id+"F13.wireOp",EDGE,"E64.bottom"),sQuery(id+"F13.wireOp",EDGE,"E64.top"),sQuery(id+"F13.wireOp",EDGE,"E64.left"),sQuery(id+"F13.wireOp",EDGE,"E64.right"),sQuery(id+"F13.wireOp",EDGE,"E78.bottom"),sQuery(id+"F13.wireOp",EDGE,"E78.top"),sQuery(id+"F13.wireOp",EDGE,"E78.left"),sQuery(id+"F13.wireOp",EDGE,"E78.right"),sQuery(id+"F13.wireOp",EDGE,"E79.bottom"),sQuery(id+"F13.wireOp",EDGE,"E79.top"),sQuery(id+"F13.wireOp",EDGE,"E79.left"),sQuery(id+"F13.wireOp",EDGE,"E79.right"),sQuery(id+"F13.wireOp",EDGE,"E84"),sQuery(id+"F13.wireOp",EDGE,"E85"),subQ0])],"isStart":false})});}
            extrude(context, id + "F17", {"entities" : qUnion([Q0]), "operationType" : NewBodyOperationType.ADD, "depth" : (5.6 - 2.5) * mm});
        }
        {
            var Q0;
            Q0=makeQuery(id+"F17.opExtrude","CAP_FACE",FACE,{"disambiguationData":[OSD([sQuery(id+"F13.wireOp",EDGE,"E64.bottom"),sQuery(id+"F13.wireOp",EDGE,"E64.top"),sQuery(id+"F13.wireOp",EDGE,"E64.left"),sQuery(id+"F13.wireOp",EDGE,"E64.right"),sQuery(id+"F13.wireOp",EDGE,"E78.bottom"),sQuery(id+"F13.wireOp",EDGE,"E78.top"),sQuery(id+"F13.wireOp",EDGE,"E78.left"),sQuery(id+"F13.wireOp",EDGE,"E78.right"),sQuery(id+"F13.wireOp",EDGE,"E79.bottom"),sQuery(id+"F13.wireOp",EDGE,"E79.top"),sQuery(id+"F13.wireOp",EDGE,"E79.left"),sQuery(id+"F13.wireOp",EDGE,"E79.right"),sQuery(id+"F13.wireOp",EDGE,"E84"),sQuery(id+"F13.wireOp",EDGE,"E85"),sQuery(id+"F13.wireOp",EDGE,"E86")])],"isStart":false});
            extrude(context, id + "F18", {"entities" : qUnion([Q0]), "operationType" : NewBodyOperationType.REMOVE, "oppositeDirection" : true, "depth" : .2 * mm});
        }
        {
            var Q0;
            Q0=makeQuery(id+"F16.opExtrude","CAP_FACE",FACE,{"disambiguationData":[OSD([sQuery(id+"F15.wireOp",EDGE,"E88.0"),sQuery(id+"F15.wireOp",EDGE,"E89.0"),sQuery(id+"F15.wireOp",EDGE,"E90.0"),sQuery(id+"F15.wireOp",EDGE,"E91.0"),sQuery(id+"F15.wireOp",EDGE,"E92.0"),sQuery(id+"F15.wireOp",EDGE,"E93.0"),sQuery(id+"F15.wireOp",EDGE,"E94.0"),sQuery(id+"F15.wireOp",EDGE,"E95.0"),sQuery(id+"F15.wireOp",EDGE,"E96.0"),sQuery(id+"F15.wireOp",EDGE,"E97.0"),sQuery(id+"F15.wireOp",EDGE,"E98.0.0"),sQuery(id+"F15.wireOp",EDGE,"E98.0.1"),sQuery(id+"F15.wireOp",EDGE,"E98.0.2"),sQuery(id+"F15.wireOp",EDGE,"E98.0.3"),sQuery(id+"F15.wireOp",EDGE,"E99.0"),sQuery(id+"F15.wireOp",EDGE,"E100.0"),sQuery(id+"F15.wireOp",EDGE,"E101")])],"isStart":false});
            var sketch = newSketch(context, id + "F19", { "sketchPlane" : qUnion([Q0])});
            skText(sketch, "E102", { "text": "V2.10", "fontName": "OpenSans-Bold.ttf"});
            const initialGuessF19  = {"E102": [0.08223, 0.03019, 1, 0, 0.00538]};
            skSetInitialGuess(sketch, initialGuessF19);
            skSolve(sketch);
        }
        {
            var Q0;
            Q0 = qSketchRegion(id + "F19", true);
            extrude(context, id + "F20", {"entities" : qUnion([Q0]), "operationType" : NewBodyOperationType.REMOVE, "oppositeDirection" : true, "depth" : .4 * mm});
        }
        {
            var Q0;
            Q0=qCreatedBy(makeId("Top.planeOp"),FACE);
            var sketch = newSketch(context, id + "F21", { "sketchPlane" : qUnion([Q0])});
            skLineSegment(sketch, "E103.bottom", {"start": v(76.23, -69.7) * mm, "end": v(131.23, -69.7) * mm});
            skLineSegment(sketch, "E103.top", {"start": v(76.23, -111.7) * mm, "end": v(131.23, -111.7) * mm});
            skLineSegment(sketch, "E103.left", {"start": v(76.23, -69.7) * mm, "end": v(76.23, -111.7) * mm});
            skLineSegment(sketch, "E103.right", {"start": v(131.23, -69.7) * mm, "end": v(131.23, -111.7) * mm});
            skLineSegment(sketch, "E104", {"start": v(76.23, -69.7) * mm, "end": v(76.23, -77.7) * mm, "construction": true});
            skLineSegment(sketch, "E105", {"start": v(76.23, -77.7) * mm, "end": v(86.23, -77.7) * mm, "construction": true});
            skLineSegment(sketch, "E106", {"start": v(86.23, -77.7) * mm, "end": v(86.23, -103.7) * mm, "construction": true});
            skLineSegment(sketch, "E107", {"start": v(86.23, -103.7) * mm, "end": v(86.23, -111.7) * mm, "construction": true});
            skLineSegment(sketch, "E108", {"start": v(86.23, -111.7) * mm, "end": v(104.23, -111.7) * mm, "construction": true});
            skLineSegment(sketch, "E109", {"start": v(104.23, -111.7) * mm, "end": v(104.23, -101.7) * mm, "construction": true});
            skLineSegment(sketch, "E110", {"start": v(104.23, -111.7) * mm, "end": v(125.23, -111.7) * mm, "construction": true});
            skLineSegment(sketch, "E111", {"start": v(125.23, -111.7) * mm, "end": v(125.23, -104.7) * mm, "construction": true});
            skCircle(sketch, "E112", {"center": v(86.23, -77.7) * mm, "radius": 2 * mm});
            skCircle(sketch, "E113", {"center": v(86.23, -103.7) * mm, "radius": 2 * mm});
            skCircle(sketch, "E114", {"center": v(104.23, -101.7) * mm, "radius": 2 * mm});
            skLineSegment(sketch, "E115.bottom", {"start": v(80.38, -84.3) * mm, "end": v(92.08, -84.3) * mm});
            skLineSegment(sketch, "E115.top", {"start": v(80.38, -97.1) * mm, "end": v(92.08, -97.1) * mm});
            skLineSegment(sketch, "E115.left", {"start": v(80.38, -84.3) * mm, "end": v(80.38, -97.1) * mm});
            skLineSegment(sketch, "E115.right", {"start": v(92.08, -84.3) * mm, "end": v(92.08, -97.1) * mm});
            skPoint(sketch, "E116", {"position": v(86.23, -90.7) * mm});
            skPoint(sketch, "E117", {"position": v(80.38, -90.7) * mm});
            skPoint(sketch, "E118", {"position": v(86.23, -84.3) * mm});
            skLineSegment(sketch, "E119.bottom", {"start": v(125.23, -104.7) * mm, "end": v(111.43, -104.7) * mm});
            skLineSegment(sketch, "E119.top", {"start": v(125.23, -76.1) * mm, "end": v(111.43, -76.1) * mm});
            skLineSegment(sketch, "E119.left", {"start": v(125.23, -104.7) * mm, "end": v(125.23, -76.1) * mm});
            skLineSegment(sketch, "E119.right", {"start": v(111.43, -104.7) * mm, "end": v(111.43, -76.1) * mm});
            skSolve(sketch);
        }
        {
            var Q0;
            Q0 = qSketchRegion(id + "F21", true);
            extrude(context, id + "F22", {"entities" : qUnion([Q0]), "depth" : 1.5 * mm});
        }
        {
            var Q0;
            Q0=makeQuery(id+"F22.opExtrude","CAP_FACE",FACE,{"disambiguationData":[OSD([sQuery(id+"F21.wireOp",EDGE,"E103.bottom"),sQuery(id+"F21.wireOp",EDGE,"E103.top"),sQuery(id+"F21.wireOp",EDGE,"E103.left"),sQuery(id+"F21.wireOp",EDGE,"E103.right"),sQuery(id+"F21.wireOp",EDGE,"E112"),sQuery(id+"F21.wireOp",EDGE,"E113"),sQuery(id+"F21.wireOp",EDGE,"E114"),sQuery(id+"F21.wireOp",EDGE,"E115.bottom"),sQuery(id+"F21.wireOp",EDGE,"E115.top"),sQuery(id+"F21.wireOp",EDGE,"E115.left"),sQuery(id+"F21.wireOp",EDGE,"E115.right"),sQuery(id+"F21.wireOp",EDGE,"E119.bottom"),sQuery(id+"F21.wireOp",EDGE,"E119.top"),sQuery(id+"F21.wireOp",EDGE,"E119.left"),sQuery(id+"F21.wireOp",EDGE,"E119.right")])],"isStart":true});
            var sketch = newSketch(context, id + "F23", { "sketchPlane" : qUnion([Q0])});
            skText(sketch, "E120", { "text": "V2.10", "fontName": "OpenSans-Regular.ttf"});
            const initialGuessF23  = {"E120": [0.08968, 0.07476, 1, 0, 0.00548]};
            skSetInitialGuess(sketch, initialGuessF23);
            skSolve(sketch);
        }
        {
            var Q0;
            Q0 = qSketchRegion(id + "F23", true);
            extrude(context, id + "F24", {"entities" : qUnion([Q0]), "operationType" : NewBodyOperationType.REMOVE, "oppositeDirection" : true, "depth" : .6 * mm});
        }
        {
            var Q0;
            Q0=makeQuery(id+"F24.boolean.opBoolean","COPY",FACE,{"derivedFrom":makeQuery(id+"F24.opExtrude","CAP_FACE",FACE,{"disambiguationData":[OSD([sQuery(id+"F23.wireOp",EDGE,"E120.sketch_text.stroke-46"),sQuery(id+"F23.wireOp",EDGE,"E120.sketch_text.stroke-47"),sQuery(id+"F23.wireOp",EDGE,"E120.sketch_text.stroke-48"),sQuery(id+"F23.wireOp",EDGE,"E120.sketch_text.stroke-49"),sQuery(id+"F23.wireOp",EDGE,"E120.sketch_text.stroke-50"),sQuery(id+"F23.wireOp",EDGE,"E120.sketch_text.stroke-51"),sQuery(id+"F23.wireOp",EDGE,"E120.sketch_text.stroke-52"),sQuery(id+"F23.wireOp",EDGE,"E120.sketch_text.stroke-53"),sQuery(id+"F23.wireOp",EDGE,"E120.sketch_text.stroke-54"),sQuery(id+"F23.wireOp",EDGE,"E120.sketch_text.stroke-55"),sQuery(id+"F23.wireOp",EDGE,"E120.sketch_text.stroke-56"),sQuery(id+"F23.wireOp",EDGE,"E120.sketch_text.stroke-57"),sQuery(id+"F23.wireOp",EDGE,"E120.sketch_text.stroke-58"),sQuery(id+"F23.wireOp",EDGE,"E120.sketch_text.stroke-59"),sQuery(id+"F23.wireOp",EDGE,"E120.sketch_text.stroke-60"),sQuery(id+"F23.wireOp",EDGE,"E120.sketch_text.stroke-61")])],"isStart":false})});
            var Q1;
            Q1=makeQuery(id+"F24.boolean.opBoolean","COPY",FACE,{"derivedFrom":makeQuery(id+"F24.opExtrude","CAP_FACE",FACE,{"disambiguationData":[OSD([sQuery(id+"F23.wireOp",EDGE,"E120.sketch_text.stroke-37"),sQuery(id+"F23.wireOp",EDGE,"E120.sketch_text.stroke-38"),sQuery(id+"F23.wireOp",EDGE,"E120.sketch_text.stroke-39"),sQuery(id+"F23.wireOp",EDGE,"E120.sketch_text.stroke-40"),sQuery(id+"F23.wireOp",EDGE,"E120.sketch_text.stroke-41"),sQuery(id+"F23.wireOp",EDGE,"E120.sketch_text.stroke-42"),sQuery(id+"F23.wireOp",EDGE,"E120.sketch_text.stroke-43"),sQuery(id+"F23.wireOp",EDGE,"E120.sketch_text.stroke-44"),sQuery(id+"F23.wireOp",EDGE,"E120.sketch_text.stroke-45")])],"isStart":false})});
            var Q2;
            Q2=makeQuery(id+"F24.boolean.opBoolean","COPY",FACE,{"derivedFrom":makeQuery(id+"F24.opExtrude","CAP_FACE",FACE,{"disambiguationData":[OSD([sQuery(id+"F23.wireOp",EDGE,"E120.sketch_text.stroke-29"),sQuery(id+"F23.wireOp",EDGE,"E120.sketch_text.stroke-30"),sQuery(id+"F23.wireOp",EDGE,"E120.sketch_text.stroke-31"),sQuery(id+"F23.wireOp",EDGE,"E120.sketch_text.stroke-32"),sQuery(id+"F23.wireOp",EDGE,"E120.sketch_text.stroke-33"),sQuery(id+"F23.wireOp",EDGE,"E120.sketch_text.stroke-34"),sQuery(id+"F23.wireOp",EDGE,"E120.sketch_text.stroke-35"),sQuery(id+"F23.wireOp",EDGE,"E120.sketch_text.stroke-36")])],"isStart":false})});
            var Q3;
            Q3=makeQuery(id+"F24.boolean.opBoolean","COPY",FACE,{"derivedFrom":makeQuery(id+"F24.opExtrude","CAP_FACE",FACE,{"disambiguationData":[OSD([sQuery(id+"F23.wireOp",EDGE,"E120.sketch_text.stroke-9"),sQuery(id+"F23.wireOp",EDGE,"E120.sketch_text.stroke-10"),sQuery(id+"F23.wireOp",EDGE,"E120.sketch_text.stroke-11"),sQuery(id+"F23.wireOp",EDGE,"E120.sketch_text.stroke-12"),sQuery(id+"F23.wireOp",EDGE,"E120.sketch_text.stroke-13"),sQuery(id+"F23.wireOp",EDGE,"E120.sketch_text.stroke-14"),sQuery(id+"F23.wireOp",EDGE,"E120.sketch_text.stroke-15"),sQuery(id+"F23.wireOp",EDGE,"E120.sketch_text.stroke-16"),sQuery(id+"F23.wireOp",EDGE,"E120.sketch_text.stroke-17"),sQuery(id+"F23.wireOp",EDGE,"E120.sketch_text.stroke-18"),sQuery(id+"F23.wireOp",EDGE,"E120.sketch_text.stroke-19"),sQuery(id+"F23.wireOp",EDGE,"E120.sketch_text.stroke-20"),sQuery(id+"F23.wireOp",EDGE,"E120.sketch_text.stroke-21"),sQuery(id+"F23.wireOp",EDGE,"E120.sketch_text.stroke-22"),sQuery(id+"F23.wireOp",EDGE,"E120.sketch_text.stroke-23"),sQuery(id+"F23.wireOp",EDGE,"E120.sketch_text.stroke-24"),sQuery(id+"F23.wireOp",EDGE,"E120.sketch_text.stroke-25"),sQuery(id+"F23.wireOp",EDGE,"E120.sketch_text.stroke-26"),sQuery(id+"F23.wireOp",EDGE,"E120.sketch_text.stroke-27"),sQuery(id+"F23.wireOp",EDGE,"E120.sketch_text.stroke-28")])],"isStart":false})});
            var Q4;
            Q4=makeQuery(id+"F24.boolean.opBoolean","COPY",FACE,{"derivedFrom":makeQuery(id+"F24.opExtrude","CAP_FACE",FACE,{"disambiguationData":[OSD([sQuery(id+"F23.wireOp",EDGE,"E120.sketch_text.stroke-0"),sQuery(id+"F23.wireOp",EDGE,"E120.sketch_text.stroke-1"),sQuery(id+"F23.wireOp",EDGE,"E120.sketch_text.stroke-2"),sQuery(id+"F23.wireOp",EDGE,"E120.sketch_text.stroke-3"),sQuery(id+"F23.wireOp",EDGE,"E120.sketch_text.stroke-4"),sQuery(id+"F23.wireOp",EDGE,"E120.sketch_text.stroke-5"),sQuery(id+"F23.wireOp",EDGE,"E120.sketch_text.stroke-6"),sQuery(id+"F23.wireOp",EDGE,"E120.sketch_text.stroke-7"),sQuery(id+"F23.wireOp",EDGE,"E120.sketch_text.stroke-8")])],"isStart":false})});
            chamfer(context, id + "F25", {"entities" : qUnion([Q0, Q1, Q2, Q3, Q4]), "chamferType" : ChamferType.TWO_OFFSETS, "width1" : .6 * mm, "oppositeDirection" : false, "width2" : .13 * mm, "tangentPropagation" : true});
        }
    });
